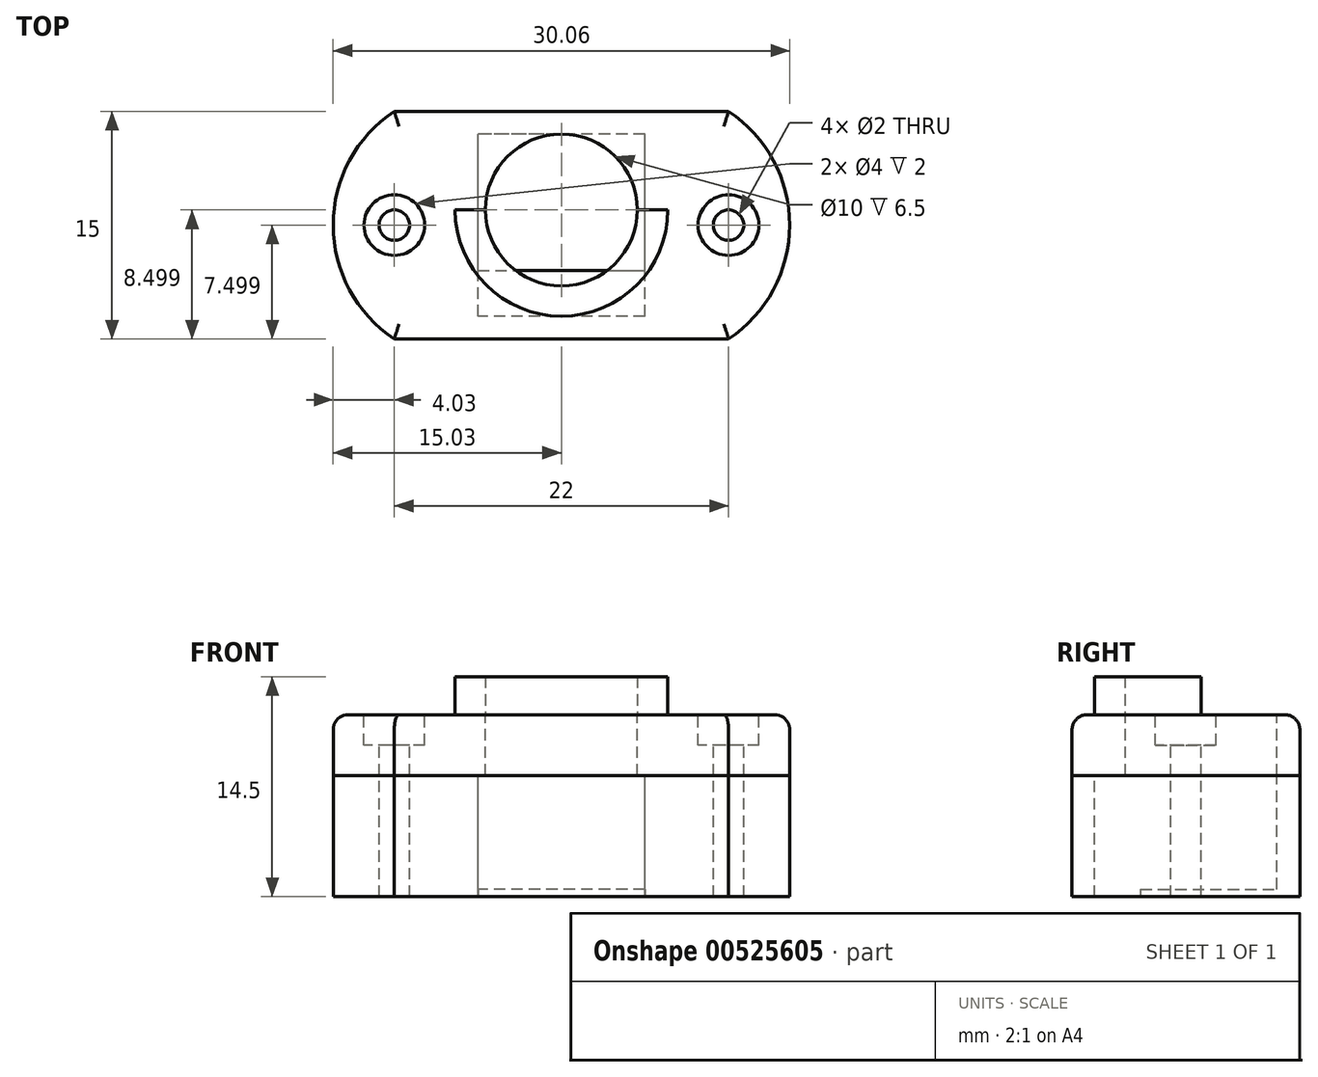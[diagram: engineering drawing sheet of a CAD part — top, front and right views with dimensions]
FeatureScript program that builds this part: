
annotation { "Feature Type Name" : "Feature", "Feature Type Description" : "" }
export const myFeature = defineFeature(function(context is Context, id is Id, definition is map)
    precondition{}
    {
        {
            var Q0;
            Q0=qCreatedBy(makeId("Top.planeOp"),FACE);
            var sketch = newSketch(context, id + "F0", { "sketchPlane" : qUnion([Q0])});
            skLineSegment(sketch, "E0.top", {"start": v(-34, -36.04) * mm, "end": v(-56, -36.04) * mm});
            skLineSegment(sketch, "E0.left", {"start": v(-34, -51.04) * mm, "end": v(-34, -36.04) * mm});
            skLineSegment(sketch, "E0.right", {"start": v(-56, -51.04) * mm, "end": v(-56, -36.04) * mm});
            skPoint(sketch, "E0.middle", {"position": v(-45, -43.54) * mm});
            skArc(sketch, "E1", {"start": v(-34, -51.04) * mm, "mid": v(-29.97, -43.54) * mm, "end": v(-34, -36.04) * mm});
            skArc(sketch, "E2", {"start": v(-56, -36.04) * mm, "mid": v(-60.03, -43.54) * mm, "end": v(-56, -51.04) * mm});
            skLineSegment(sketch, "E3", {"start": v(-56, -51.04) * mm, "end": v(-34, -51.04) * mm});
            skSolve(sketch);
        }
        {
            var Q0;
            Q0=qSketchRegion(id+"F0",true);
            extrude(context, id + "F1", {"entities" : qUnion([Q0]), "depth" : 8 * mm, "offsetDistance" : 25 * mm});
        }
        {
            var Q0;
            Q0=makeQuery(id+"F1.opExtrude","CAP_FACE",FACE,{"disambiguationData":[OSD([sQuery(id+"F0.wireOp",EDGE,"E0.bottom"),sQuery(id+"F0.wireOp",EDGE,"E0.top"),sQuery(id+"F0.wireOp",EDGE,"E0.left"),sQuery(id+"F0.wireOp",EDGE,"E0.right")])],"isStart":false});
            var sketch = newSketch(context, id + "F2", { "sketchPlane" : qUnion([Q0])});
            skCircle(sketch, "E4", {"center": v(-56, -43.54) * mm, "radius": 1 * mm});
            skCircle(sketch, "E5", {"center": v(-34, -43.54) * mm, "radius": 1 * mm});
            skCircle(sketch, "E6", {"center": v(-45, -43.54) * mm, "radius": 3.55 * mm, "construction": true});
            skLineSegment(sketch, "E7.bottom", {"start": v(-39.5, -49.54) * mm, "end": v(-50.5, -49.54) * mm});
            skLineSegment(sketch, "E7.top", {"start": v(-39.5, -37.54) * mm, "end": v(-50.5, -37.54) * mm});
            skLineSegment(sketch, "E7.left", {"start": v(-39.5, -49.54) * mm, "end": v(-39.5, -37.54) * mm});
            skLineSegment(sketch, "E7.right", {"start": v(-50.5, -49.54) * mm, "end": v(-50.5, -37.54) * mm});
            skSolve(sketch);
        }
        {
            var Q0;
            Q0=qSketchRegion(id+"F2",true);
            extrude(context, id + "F3", {"entities" : qUnion([Q0]), "operationType" : NewBodyOperationType.REMOVE, "oppositeDirection" : true, "depth" : 9 * mm, "offsetDistance" : 25 * mm});
        }
        {
            var Q0;
            Q0=makeQuery(id+"F1.opExtrude","CAP_FACE",FACE,{"disambiguationData":[OSD([sQuery(id+"F0.wireOp",EDGE,"E0.top"),sQuery(id+"F0.wireOp",EDGE,"E1"),sQuery(id+"F0.wireOp",EDGE,"E2"),sQuery(id+"F0.wireOp",EDGE,"E3")])],"isStart":true});
            var sketch = newSketch(context, id + "F4", { "sketchPlane" : qUnion([Q0])});
            skLineSegment(sketch, "E8.bottom", {"start": v(-50.5, 37.54) * mm, "end": v(-39.5, 37.54) * mm});
            skLineSegment(sketch, "E8.top", {"start": v(-50.5, 46.54) * mm, "end": v(-39.5, 46.54) * mm});
            skLineSegment(sketch, "E8.left", {"start": v(-50.5, 37.54) * mm, "end": v(-50.5, 46.54) * mm});
            skLineSegment(sketch, "E8.right", {"start": v(-39.5, 37.54) * mm, "end": v(-39.5, 46.54) * mm});
            skSolve(sketch);
        }
        {
            var Q0;
            Q0=qSketchRegion(id+"F4",true);
            extrude(context, id + "F5", {"entities" : qUnion([Q0]), "operationType" : NewBodyOperationType.ADD, "oppositeDirection" : true, "depth" : 0.5 * mm, "offsetDistance" : 25 * mm});
        }
        {
            var Q0;
            Q0=makeQuery(id+"F1.opExtrude","CAP_FACE",FACE,{"disambiguationData":[OSD([sQuery(id+"F0.wireOp",EDGE,"E0.top"),sQuery(id+"F0.wireOp",EDGE,"E1"),sQuery(id+"F0.wireOp",EDGE,"E2"),sQuery(id+"F0.wireOp",EDGE,"E3")])],"isStart":false});
            var sketch = newSketch(context, id + "F6", { "sketchPlane" : qUnion([Q0])});
            skLineSegment(sketch, "E9.top", {"start": v(-34, -36.04) * mm, "end": v(-56, -36.04) * mm});
            skLineSegment(sketch, "E9.left", {"start": v(-34, -51.04) * mm, "end": v(-34, -36.04) * mm});
            skLineSegment(sketch, "E9.right", {"start": v(-56, -51.04) * mm, "end": v(-56, -36.04) * mm});
            skPoint(sketch, "E9.middle", {"position": v(-45, -43.54) * mm});
            skArc(sketch, "E10", {"start": v(-34, -51.04) * mm, "mid": v(-29.97, -43.54) * mm, "end": v(-34, -36.04) * mm});
            skArc(sketch, "E11", {"start": v(-56, -36.04) * mm, "mid": v(-60.03, -43.54) * mm, "end": v(-56, -51.04) * mm});
            skLineSegment(sketch, "E12", {"start": v(-56, -51.04) * mm, "end": v(-34, -51.04) * mm});
            skPoint(sketch, "E13", {"position": v(-39.5, -43.54) * mm});
            skPoint(sketch, "E14", {"position": v(-45, -37.54) * mm});
            skSolve(sketch);
        }
        {
            var Q0;
            Q0=qSketchRegion(id+"F6",true);
            extrude(context, id + "F7", {"entities" : qUnion([Q0]), "depth" : 4 * mm, "offsetDistance" : 25 * mm});
        }
        {
            var Q0;
            Q0=makeQuery(id+"F7.opExtrude","CAP_FACE",FACE,{"disambiguationData":[OSD([sQuery(id+"F6.wireOp",EDGE,"E9.top"),sQuery(id+"F6.wireOp",EDGE,"E10"),sQuery(id+"F6.wireOp",EDGE,"E11"),sQuery(id+"F6.wireOp",EDGE,"E12")])],"isStart":false});
            var sketch = newSketch(context, id + "F8", { "sketchPlane" : qUnion([Q0])});
            skCircle(sketch, "E15", {"center": v(-56, -43.54) * mm, "radius": 1 * mm, "construction": true});
            skCircle(sketch, "E16", {"center": v(-34, -43.54) * mm, "radius": 1 * mm, "construction": true});
            skPoint(sketch, "E17", {"position": v(-29.97, -43.54) * mm});
            skPoint(sketch, "E18", {"position": v(-45, -51.04) * mm});
            skCircle(sketch, "E19", {"center": v(-45, -42.54) * mm, "radius": 5 * mm});
            skLineSegment(sketch, "E20.0", {"start": v(-39.5, -37.54) * mm, "end": v(-50.5, -37.54) * mm});
            skSolve(sketch);
        }
        {
            var Q0;
            Q0=qSketchRegion(id+"F8",true);
            extrude(context, id + "F9", {"entities" : qUnion([Q0]), "operationType" : NewBodyOperationType.REMOVE, "oppositeDirection" : true, "depth" : 4 * mm, "offsetDistance" : 25 * mm});
        }
        {
            var Q0;
            Q0=makeQuery(id+"F7.opExtrude","CAP_EDGE",EDGE,{"disambiguationData":[OSD([sQuery(id+"F6.wireOp",EDGE,"E10")])],"isStart":false});
            var Q1;
            Q1=makeQuery(id+"F7.opExtrude","CAP_EDGE",EDGE,{"disambiguationData":[OSD([sQuery(id+"F6.wireOp",EDGE,"E9.top")])],"isStart":false});
            var Q2;
            Q2=makeQuery(id+"F7.opExtrude","CAP_EDGE",EDGE,{"disambiguationData":[OSD([sQuery(id+"F6.wireOp",EDGE,"E11")])],"isStart":false});
            var Q3;
            Q3=makeQuery(id+"F7.opExtrude","CAP_EDGE",EDGE,{"disambiguationData":[OSD([sQuery(id+"F6.wireOp",EDGE,"E12")])],"isStart":false});
            fillet(context, id + "F10", {"entities" : qUnion([Q0, Q1, Q2, Q3]), "radius" : 1 * mm, "tangentPropagation" : true, "defaultsChanged" : true, "vertexSettings" : [], "allowEdgeOverflow" : false});
        }
        {
            var Q0;
            Q0=sQuery(id+"F8.wireOp",VERTEX,"E16.center");
            var Q1;
            Q1=sQuery(id+"F8.wireOp",VERTEX,"E15.center");
            var Q2;
            Q2=makeQuery(id+"F7.opExtrude","SWEPT_BODY",BODY,{"disambiguationData":[OSD([sQuery(id+"F6.wireOp",EDGE,"E9.top"),sQuery(id+"F6.wireOp",EDGE,"E10"),sQuery(id+"F6.wireOp",EDGE,"E11"),sQuery(id+"F6.wireOp",EDGE,"E12")])]});
            hole(context, id + "F11", {"style" : HoleStyle.C_BORE, "endStyle" : HoleEndStyle.BLIND, "holeDiameter" : 2 * mm, "cBoreDiameter" : 4 * mm, "cBoreDepth" : 2 * mm, "majorDiameter" : 5 * mm, "holeDepth" : 20 * mm, "tappedDepth" : 12 * mm, "tapClearance" : 3, "locations" : qUnion([Q0, Q1]), "scope" : qUnion([Q2])});
        }
        {
            var Q0;
            Q0=makeQuery(id+"F7.opExtrude","CAP_FACE",FACE,{"disambiguationData":[OSD([sQuery(id+"F6.wireOp",EDGE,"E9.top"),sQuery(id+"F6.wireOp",EDGE,"E10"),sQuery(id+"F6.wireOp",EDGE,"E11"),sQuery(id+"F6.wireOp",EDGE,"E12")])],"isStart":false});
            var sketch = newSketch(context, id + "F12", { "sketchPlane" : qUnion([Q0])});
            skPoint(sketch, "E21", {"position": v(-45, -42.54) * mm});
            skLineSegment(sketch, "E22", {"start": v(-45, -42.54) * mm, "end": v(-45, -46.97) * mm, "construction": true});
            skLineSegment(sketch, "E23", {"start": v(-45, -42.54) * mm, "end": v(-50, -42.54) * mm, "construction": true});
            skLineSegment(sketch, "E24", {"start": v(-45, -42.54) * mm, "end": v(-40, -42.54) * mm, "construction": true});
            skArc(sketch, "E25", {"start": v(-50, -42.54) * mm, "mid": v(-45, -47.54) * mm, "end": v(-40, -42.54) * mm});
            skLineSegment(sketch, "E26", {"start": v(-50, -42.54) * mm, "end": v(-52, -42.54) * mm});
            skLineSegment(sketch, "E27", {"start": v(-40, -42.54) * mm, "end": v(-38, -42.54) * mm});
            skArc(sketch, "E28", {"start": v(-52, -42.54) * mm, "mid": v(-45, -49.54) * mm, "end": v(-38, -42.54) * mm});
            skSolve(sketch);
        }
        {
            var Q0;
            Q0 = qSketchRegion(id + "F12", true);
            extrude(context, id + "F13", {"entities" : qUnion([Q0]), "operationType" : NewBodyOperationType.ADD, "depth" : 2.5 * mm, "offsetDistance" : 25 * mm});
        }
    });
